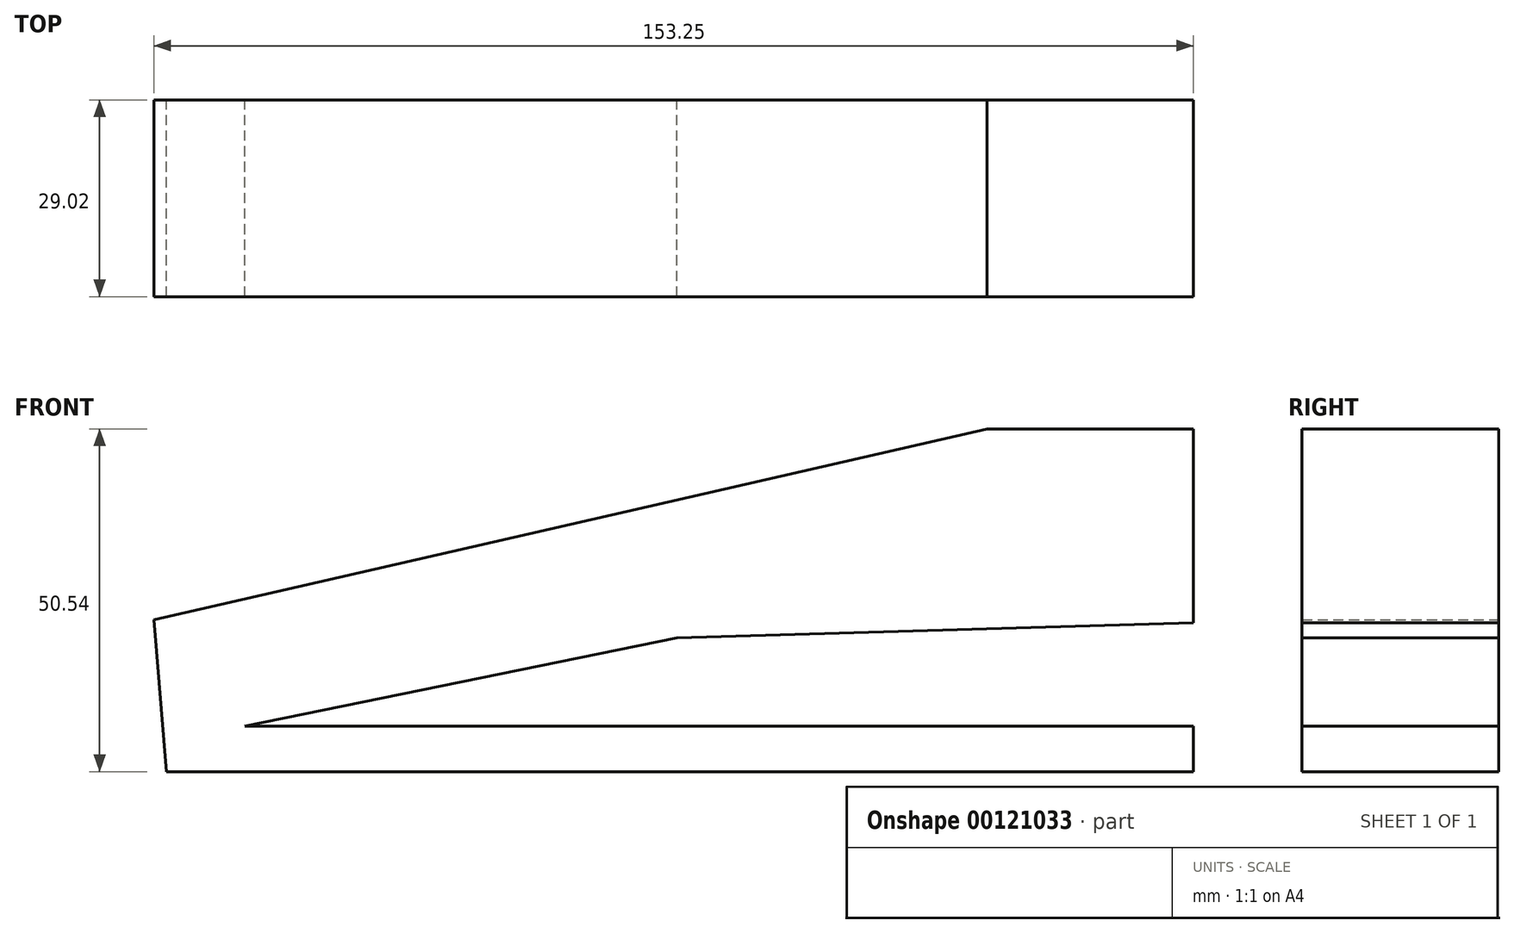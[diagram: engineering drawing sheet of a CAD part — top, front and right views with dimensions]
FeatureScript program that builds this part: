
annotation { "Feature Type Name" : "Feature", "Feature Type Description" : "" }
export const myFeature = defineFeature(function(context is Context, id is Id, definition is map)
    precondition{}
    {
        {
            var Q0;
            Q0=qCreatedBy(makeId("Front.planeOp"),FACE);
            var sketch = newSketch(context, id + "F0", { "sketchPlane" : qUnion([Q0])});
            skLineSegment(sketch, "E0", {"start": v(-75.24, 0) * mm, "end": v(76.16, 0) * mm});
            skLineSegment(sketch, "E1", {"start": v(76.16, 0) * mm, "end": v(76.16, 6.7) * mm});
            skLineSegment(sketch, "E2", {"start": v(76.16, 6.7) * mm, "end": v(-63.7, 6.7) * mm});
            skLineSegment(sketch, "E3", {"start": v(-63.7, 6.7) * mm, "end": v(76.16, 35.31) * mm});
            skLineSegment(sketch, "E4", {"start": v(76.16, 35.31) * mm, "end": v(76.16, 50.54) * mm});
            skLineSegment(sketch, "E5", {"start": v(76.16, 50.54) * mm, "end": v(45.7, 50.54) * mm});
            skLineSegment(sketch, "E6", {"start": v(45.7, 50.54) * mm, "end": v(-77.09, 22.39) * mm});
            skLineSegment(sketch, "E7", {"start": v(-77.09, 22.39) * mm, "end": v(-75.24, 0) * mm});
            skLineSegment(sketch, "E8", {"start": v(76.16, 35.31) * mm, "end": v(76.16, 21.93) * mm});
            skLineSegment(sketch, "E9", {"start": v(76.16, 21.93) * mm, "end": v(0, 19.73) * mm});
            skSolve(sketch);
        }
        {
            var Q0;
            {var subQ0=sQuery(id+"F0.wireOp",EDGE,"E8");Q0=makeQuery(id+"F0.imprint","IMPRINT",FACE,{"disambiguationData":[TD([[makeQuery(id+"F0.imprint","IMPRINT",EDGE,{"derivedFrom":subQ0}),-1.0]])]});}
            var Q1;
            Q1=makeQuery(id+"F0.imprint","IMPRINT",FACE,{"disambiguationData":[TD([[makeQuery(id+"F0.imprint","IMPRINT",EDGE,{"derivedFrom":sQuery(id+"F0.wireOp",EDGE,"E0")}),1.0]])]});
            extrude(context, id + "F1", {"entities" : qUnion([Q0, Q1]), "depth" : 29.02 * mm});
        }
    });
